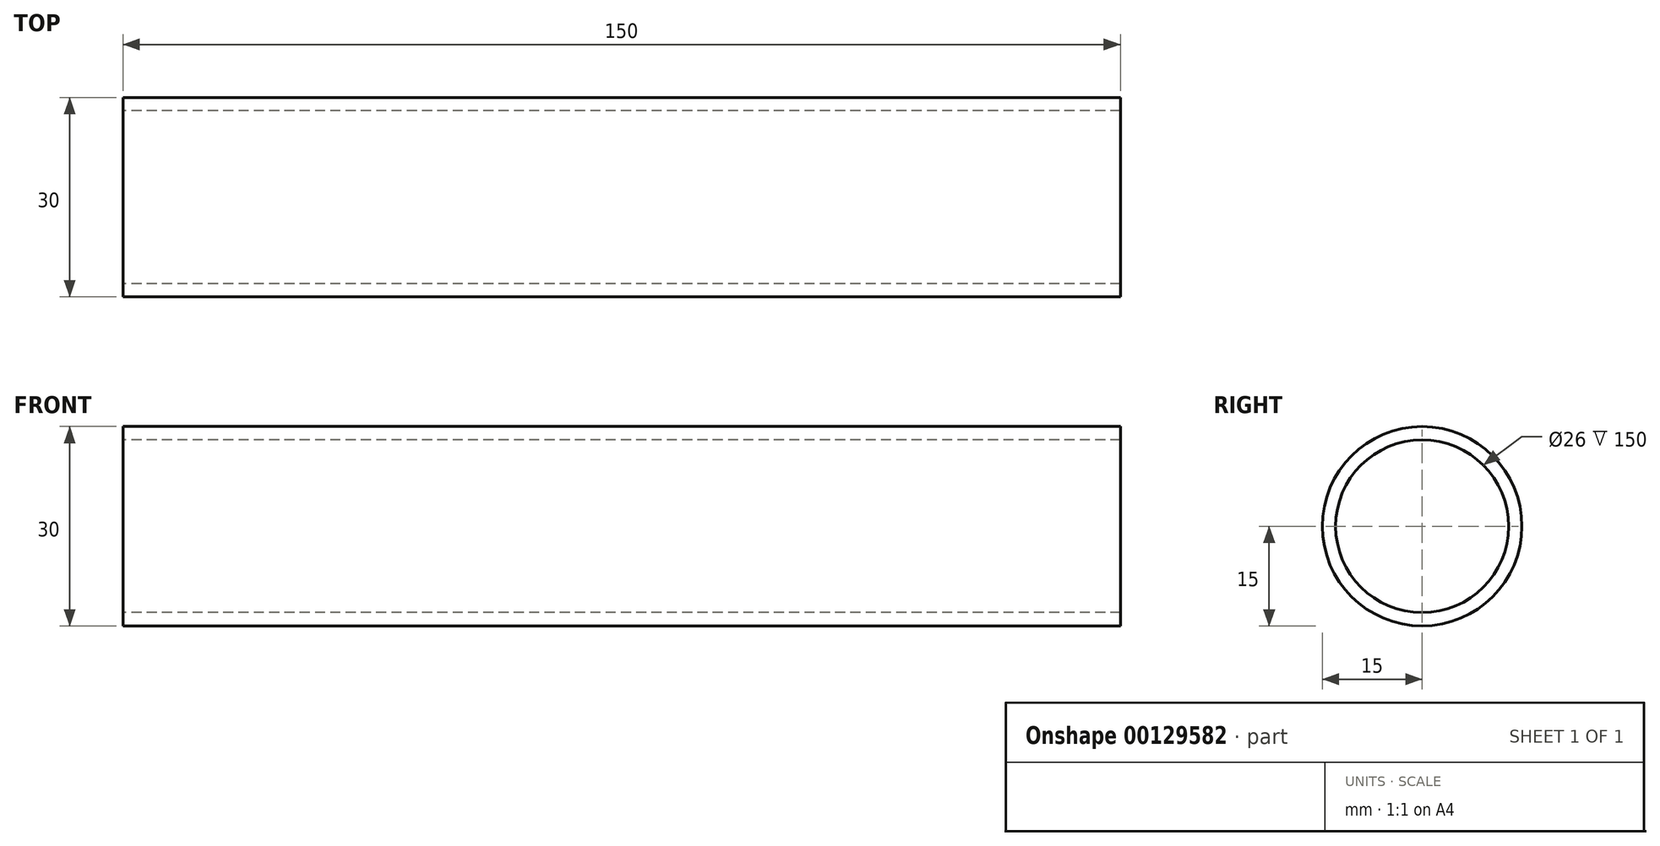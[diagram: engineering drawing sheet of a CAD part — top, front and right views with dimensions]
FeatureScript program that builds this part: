
annotation { "Feature Type Name" : "Feature", "Feature Type Description" : "" }
export const myFeature = defineFeature(function(context is Context, id is Id, definition is map)
    precondition{}
    {
        {
            var Q0;
            Q0=qCreatedBy(makeId("Right.planeOp"),FACE);
            var sketch = newSketch(context, id + "F0", { "sketchPlane" : qUnion([Q0])});
            skCircle(sketch, "E0", {"center": v(0, 0) * mm, "radius": 15 * mm});
            skCircle(sketch, "E1.0", {"center": v(0, 0) * mm, "radius": 13 * mm});
            skSolve(sketch);
        }
        {
            var Q0;
            Q0 = qSketchRegion(id + "F0", true);
            extrude(context, id + "F1", {"entities" : qUnion([Q0]), "endBound" : BoundingType.SYMMETRIC, "depth" : 150 * mm});
        }
    });
